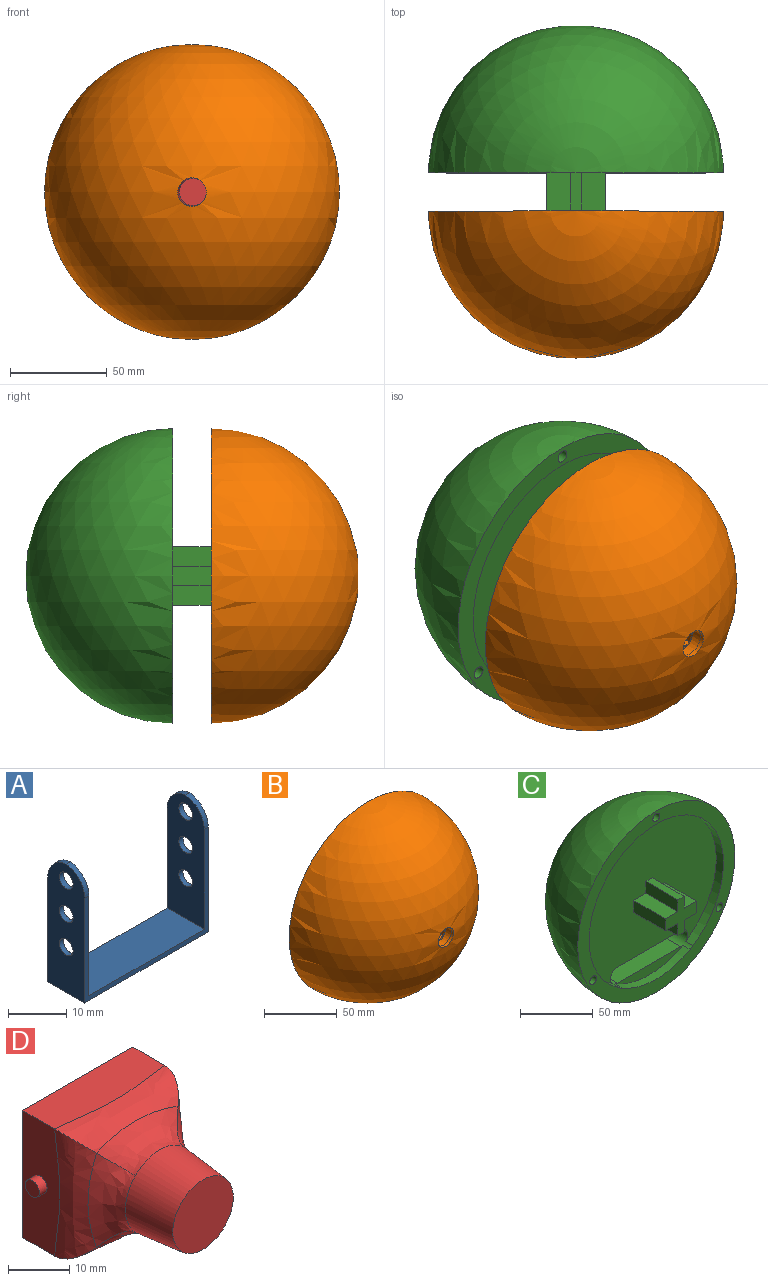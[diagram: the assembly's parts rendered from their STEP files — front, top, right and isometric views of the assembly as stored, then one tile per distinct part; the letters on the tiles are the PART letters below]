
ASSEMBLY  parts=4 mates=3
PART A: 18 faces, bbox 30x9x27 mm
  f0: plane 30x9mm, normal (0,0,-1), area 270mm2, adj f1,f5,f6,f7
  f1: plane 26.98x9mm, normal (1,0,0), area 206.6mm2, adj f0,f6,f7,f10,f11,f15,f16,f17
  f2: plane 25.98x9mm, normal (-1,0,0), area 197.6mm2, adj f3,f6,f7,f10,f11,f15,f16,f17
  f3: plane 28x9mm, normal (0,0,1), area 252mm2, adj f2,f4,f6,f7
  f4: plane 25.98x9mm, normal (1,0,0), area 197.6mm2, adj f3,f6,f7,f8,f9,f12,f13,f14
  f5: plane 26.98x9mm, normal (-1,0,0), area 206.6mm2, adj f0,f6,f7,f8,f9,f12,f13,f14
  f6: plane 30x22mm, normal (0,1,0), area 72mm2, adj f0,f1,f2,f3,f4,f5,f8,f10
  f7: plane 30x22mm, normal (0,-1,0), area 72mm2, adj f0,f1,f2,f3,f4,f5,f9,f11
  f8: cylinder r=5mm len=4.98mm, axis (1,0,0), area 7.4mm2, adj f4,f5,f6,f9
  f9: cylinder r=5mm len=4.98mm, axis (-1,0,0), area 7.4mm2, adj f4,f5,f7,f8
  f10: cylinder r=5mm len=4.98mm, axis (1,0,0), area 7.4mm2, adj f1,f2,f6,f11
  f11: cylinder r=5mm len=4.98mm, axis (-1,0,0), area 7.4mm2, adj f1,f2,f7,f10
  f12: cylinder r=1.65mm len=3.3mm, axis (-1,0,0), area 10.4mm2, adj f4,f5
  f13: cylinder r=1.65mm len=3.3mm, axis (-1,0,0), area 10.4mm2, adj f4,f5
  f14: cylinder r=1.65mm len=3.3mm, axis (-1,0,0), area 10.4mm2, adj f4,f5
  f15: cylinder r=1.65mm len=3.3mm, axis (-1,0,0), area 10.4mm2, adj f1,f2
  f16: cylinder r=1.65mm len=3.3mm, axis (-1,0,0), area 10.4mm2, adj f1,f2
  f17: cylinder r=1.65mm len=3.3mm, axis (-1,0,0), area 10.4mm2, adj f1,f2
PART B: 30 faces, bbox 152.5x76.3x152.5 mm
  f0: cone r=0mm half-angle=59deg, axis (0,1,0), area 38.7mm2, adj f1
  f1: cylinder r=3.25mm len=6.5mm, axis (0,1,0), area 102.1mm2, adj f0,f5
  f2: cone r=0mm half-angle=59deg, axis (0,1,0), area 38.7mm2, adj f3
  f3: cylinder r=3.25mm len=6.5mm, axis (0,1,0), area 102.1mm2, adj f2,f5
  f4: sphere r=76.2mm, area 36310.5mm2, adj f5,f6
  f5: plane 152.51x152.51mm, normal (0,1,0), area 5550.2mm2, adj f1,f3,f4,f21,f22,f23,f24,f25
  f6: cylinder r=7.4mm len=14.8mm, axis (0,1,0), area 101.4mm2, adj f4,f7
  f7: cone r=7.4mm half-angle=3deg, axis (0,1,0), area 262.8mm2, adj f6,f26,f27,f28,f29
  f8: bspline ~31x10.03mm, area 268mm2, adj f9,f11,f12,f27
  f9: bspline ~31x10.03mm, area 268mm2, adj f8,f10,f14,f29
  f10: bspline ~31x10.03mm, area 268mm2, adj f9,f11,f15,f28
  f11: bspline ~31x10.03mm, area 268mm2, adj f8,f10,f13,f26
  f12: plane 31x15mm, normal (-1,0,0), area 465mm2, adj f8,f13,f14,f19
  f13: plane 31x15mm, normal (0,0,1), area 465mm2, adj f11,f12,f15,f16
  f14: plane 31x15mm, normal (0,0,-1), area 465mm2, adj f9,f12,f15,f18
  f15: plane 31x15mm, normal (1,0,0), area 465mm2, adj f10,f13,f14,f17
  f16: bspline ~62.86x43.66mm, area 1226.7mm2, adj f13,f17,f19,f25
  f17: bspline ~62.86x43.66mm, area 1226.7mm2, adj f15,f16,f18,f24
  f18: bspline ~62.86x43.66mm, area 1226.7mm2, adj f14,f17,f19,f22
  f19: bspline ~49.54x25.4mm, area 1226.7mm2, adj f12,f16,f18,f23
  f20: cone r=0mm half-angle=59deg, axis (0,1,0), area 38.7mm2, adj f21
  f21: cylinder r=3.25mm len=6.5mm, axis (0,1,0), area 102.1mm2, adj f5,f20
  f22: bspline ~92.45x42.36mm, area 2543.9mm2, adj f5,f18,f23,f24
  f23: bspline ~92.45x42.36mm, area 2543.9mm2, adj f5,f19,f22,f25
  f24: bspline ~92.45x42.36mm, area 2543.9mm2, adj f5,f17,f22,f25
  f25: bspline ~92.45x42.36mm, area 2543.9mm2, adj f5,f16,f23,f24
  f26: bspline ~13.38x3.27mm, area 18.7mm2, adj f7,f11,f27,f28
  f27: bspline ~13.38x3.27mm, area 18.7mm2, adj f7,f8,f26,f29
  f28: bspline ~13.38x3.27mm, area 18.7mm2, adj f7,f10,f26,f29
  f29: bspline ~13.38x3.27mm, area 18.7mm2, adj f7,f9,f27,f28
PART C: 30 faces, bbox 152.4x100.2x152.4 mm
  f0: plane 152.4x152.4mm, normal (0,-1,0), area 4786mm2, adj f2,f4,f6,f8,f9,f12,f14,f16
  f1: plane 61.5x26mm, normal (0,0,-1), area 1599mm2, adj f2,f4,f10,f15
  f2: cylinder r=6.75mm len=33mm, axis (0,-1,0), area 575mm2, adj f0,f1,f3,f10,f13,f14,f15,f16
  f3: plane 61.5x26mm, normal (0,0,1), area 1599mm2, adj f2,f4,f10,f13
  f4: cylinder r=6.75mm len=33mm, axis (0,-1,0), area 575mm2, adj f0,f1,f3,f10,f13,f14,f15,f16
  f5: cone r=0mm half-angle=59deg, axis (0,-1,0), area 38.7mm2, adj f6
  f6: cylinder r=3.25mm len=6.5mm, axis (0,-1,0), area 102.1mm2, adj f0,f5
  f7: cone r=0mm half-angle=59deg, axis (0,-1,0), area 38.7mm2, adj f8
  f8: cylinder r=3.25mm len=6.5mm, axis (0,-1,0), area 102.1mm2, adj f0,f7
  f9: sphere r=76.2mm, area 36482.9mm2, adj f0
  f10: plane 75x13.5mm, normal (0,-1,0), area 973.4mm2, adj f1,f2,f3,f4
  f11: cone r=0mm half-angle=59deg, axis (0,-1,0), area 38.7mm2, adj f12
  f12: cylinder r=3.25mm len=6.5mm, axis (0,-1,0), area 102.1mm2, adj f0,f11
  f13: plane 65.51x8.82mm, normal (0,-1,0), area 371.4mm2, adj f2,f3,f4,f14
  f14: cylinder r=65.2mm len=65.51mm, axis (0,-1,0), area 480.4mm2, adj f0,f2,f4,f13
  f15: plane 130.4x119.82mm, normal (0,-1,0), area 11591.1mm2, adj f1,f2,f4,f16,f17,f18,f19,f20
  f16: cylinder r=65.2mm len=130.4mm, axis (0,-1,0), area 2340.3mm2, adj f0,f2,f4,f15
  f17: plane 31x12mm, normal (0,0,-1), area 372mm2, adj f15,f18,f28,f29
  f18: plane 31x10mm, normal (-1,0,0), area 310mm2, adj f15,f17,f19,f29
  f19: plane 31x6mm, normal (0,0,-1), area 186mm2, adj f15,f18,f20,f29
  f20: plane 31x10mm, normal (1,0,0), area 310mm2, adj f15,f19,f21,f29
  f21: plane 31x12mm, normal (0,0,-1), area 372mm2, adj f15,f20,f22,f29
  f22: plane 31x10mm, normal (1,0,0), area 310mm2, adj f15,f21,f23,f29
  f23: plane 31x12mm, normal (0,0,1), area 372mm2, adj f15,f22,f24,f29
  f24: plane 31x10mm, normal (1,0,0), area 310mm2, adj f15,f23,f25,f29
  f25: plane 31x6mm, normal (0,0,1), area 186mm2, adj f15,f24,f26,f29
  f26: plane 31x10mm, normal (-1,0,0), area 310mm2, adj f15,f25,f27,f29
  f27: plane 31x12mm, normal (0,0,1), area 372mm2, adj f15,f26,f28,f29
  f28: plane 31x10mm, normal (-1,0,0), area 310mm2, adj f15,f17,f27,f29
  f29: plane 30x30mm, normal (0,-1,0), area 420mm2, adj f17,f18,f19,f20,f21,f22,f23,f24
PART D: 19 faces, bbox 30.5x29x30.5 mm
  f0: bspline ~18.92x5.24mm, area 96.6mm2, adj f1,f3,f11,f14
  f1: bspline ~18.92x5.24mm, area 96.6mm2, adj f0,f2,f9,f14
  f2: bspline ~18.92x5.24mm, area 96.6mm2, adj f1,f3,f10,f14
  f3: bspline ~18.92x5.24mm, area 96.6mm2, adj f0,f2,f12,f14
  f4: plane 25.5x8.61mm, normal (0,0,1), area 207mm2, adj f5,f6,f7,f10
  f5: plane 25.5x25.5mm, normal (0,1,0), area 650.2mm2, adj f4,f6,f7,f8
  f6: plane 25.5x8.61mm, normal (-1,0,0), area 198.7mm2, adj f4,f5,f8,f9,f17
  f7: plane 25.5x8.61mm, normal (1,0,0), area 198.7mm2, adj f4,f5,f8,f12,f15
  f8: plane 25.5x8.61mm, normal (0,0,-1), area 207mm2, adj f5,f6,f7,f11
  f9: bspline ~30.51x6.6mm, area 135.1mm2, adj f1,f6,f10,f11
  f10: bspline ~30.51x6.6mm, area 135.1mm2, adj f2,f4,f9,f12
  f11: bspline ~30.51x6.6mm, area 135.1mm2, adj f0,f8,f9,f12
  f12: bspline ~30.51x6.6mm, area 135.1mm2, adj f3,f7,f10,f11
  f13: plane 14x14mm, normal (0,-1,0), area 153.9mm2, adj f14
  f14: bspline ~15.99x15.99mm, area 473.6mm2, adj f0,f1,f2,f3,f13
  f15: cylinder r=1.62mm len=3.25mm, axis (-1,0,0), area 18.4mm2, adj f7,f16
  f16: plane 3.25x3.25mm, normal (1,0,0), area 8.3mm2, adj f15
  f17: cylinder r=1.62mm len=3.25mm, axis (1,0,0), area 18.4mm2, adj f6,f18
  f18: plane 3.25x3.25mm, normal (-1,0,0), area 8.3mm2, adj f17
PLACE A rot(axis=(1,0,0),90deg) t=(0,71.66,-4.5)mm
PLACE B t=(0,75.84,0)mm
PLACE C t=(0,95.66,0)mm
PLACE D rot(axis=(-1,0,0),0deg) t=(0.45,52.16,0)mm
MATE slider C.f11 <-> B.f20  axis (0,-1,0) through (0,95.66,70.7)mm
MATE revolute D.f15 <-> A.f14  axis (1,0,0) through (15,48.16,0)mm
MATE fastened A.f0 <-> C.f16  axis (0,1,0) through (0,71.66,0)mm
